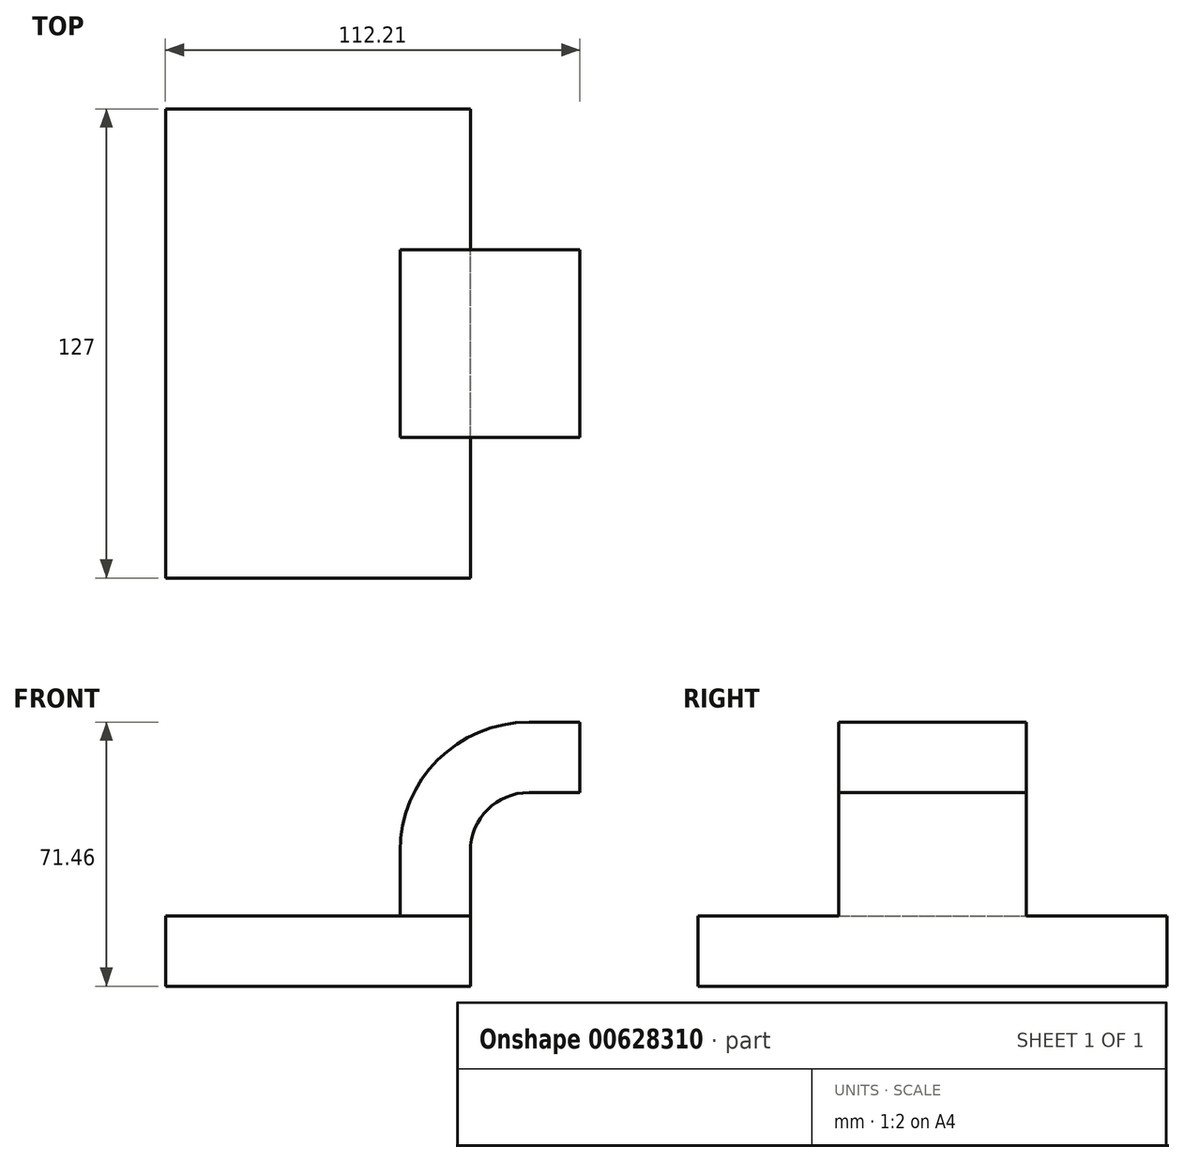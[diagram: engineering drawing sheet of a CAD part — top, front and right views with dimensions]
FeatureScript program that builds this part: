
annotation { "Feature Type Name" : "Feature", "Feature Type Description" : "" }
export const myFeature = defineFeature(function(context is Context, id is Id, definition is map)
    precondition{}
    {
        {
            var Q0;
            Q0=qCreatedBy(makeId("Front.planeOp"),FACE);
            var sketch = newSketch(context, id + "F0", { "sketchPlane" : qUnion([Q0])});
            skLineSegment(sketch, "E0.bottom", {"start": v(41.28, -9.52) * mm, "end": v(-41.28, -9.53) * mm});
            skLineSegment(sketch, "E0.top", {"start": v(41.28, 9.53) * mm, "end": v(-41.28, 9.53) * mm});
            skLineSegment(sketch, "E0.left", {"start": v(41.28, -9.52) * mm, "end": v(41.28, 9.53) * mm});
            skLineSegment(sketch, "E0.right", {"start": v(-41.28, -9.53) * mm, "end": v(-41.28, 9.53) * mm});
            skPoint(sketch, "E0.middle", {"position": v(0, 0) * mm});
            skLineSegment(sketch, "E1.bottom", {"start": v(70.93, 66.68) * mm, "end": v(121.73, 66.68) * mm});
            skLineSegment(sketch, "E1.top", {"start": v(70.93, 38.1) * mm, "end": v(121.73, 38.1) * mm});
            skLineSegment(sketch, "E1.left", {"start": v(121.73, 38.1) * mm, "end": v(121.73, 66.68) * mm});
            skLineSegment(sketch, "E1.right", {"start": v(70.93, 38.1) * mm, "end": v(70.93, 66.68) * mm});
            skPoint(sketch, "E1.middle", {"position": v(96.33, 52.39) * mm});
            skLineSegment(sketch, "E2", {"start": v(41.28, 9.53) * mm, "end": v(41.28, 27) * mm});
            skArc(sketch, "E3", {"start": v(41.27, 27) * mm, "mid": v(45.92, 38.23) * mm, "end": v(57.15, 42.88) * mm});
            skLineSegment(sketch, "E4", {"start": v(57.15, 42.88) * mm, "end": v(85.73, 42.88) * mm});
            skLineSegment(sketch, "E5.0", {"start": v(57.15, 61.93) * mm, "end": v(85.73, 61.93) * mm});
            skArc(sketch, "E5.1", {"start": v(22.23, 27) * mm, "mid": v(32.45, 51.7) * mm, "end": v(57.15, 61.93) * mm});
            skLineSegment(sketch, "E5.2", {"start": v(22.22, 9.53) * mm, "end": v(22.22, 27) * mm});
            skLineSegment(sketch, "E6", {"start": v(85.73, 42.88) * mm, "end": v(85.73, 61.93) * mm});
            skFitSpline(sketch, "E7", {"points": [v(-41.28, 9.53) * mm, v(57.15, 61.93) * mm], "startDerivative": vector(-10.9, 62.98) * mm, "endDerivative": vector(59.29, -31.03) * mm});
            skSolve(sketch);
        }
        {
            var Q0;
            {var subQ1=sQuery(id+"F0.wireOp",EDGE,"E2");Q0=makeQuery(id+"F0.imprint","IMPRINT",FACE,{"disambiguationData":[TD([[makeQuery(id+"F0.imprint","IMPRINT",EDGE,{"derivedFrom":subQ1}),1.0]])]});}
            var sketch = newSketch(context, id + "F1", { "sketchPlane" : qUnion([Q0])});
            skSolve(sketch);
        }
        {
            var Q0;
            Q0=makeQuery(id+"F0.imprint","IMPRINT",FACE,{"disambiguationData":[TD([[makeQuery(id+"F0.imprint","IMPRINT",EDGE,{"derivedFrom":sQuery(id+"F0.wireOp",EDGE,"E0.bottom")}),-1.0]])]});
            extrude(context, id + "F2", {"entities" : qUnion([Q0]), "endBound" : BoundingType.SYMMETRIC, "depth" : 127 * mm, "offsetDistance" : 25.4 * mm});
        }
        {
            var Q0;
            {var subQ1=sQuery(id+"F0.wireOp",EDGE,"E2");Q0=makeQuery(id+"F1.imprint","IMPRINT",FACE,{"disambiguationData":[TD([[makeQuery(id+"F1.imprint","IMPRINT",EDGE,{"derivedFrom":makeQuery(id+"F0.imprint","IMPRINT",EDGE,{"derivedFrom":subQ1})}),1.0]])]});}
            extrude(context, id + "F3", {"entities" : qUnion([Q0]), "operationType" : NewBodyOperationType.ADD, "endBound" : BoundingType.SYMMETRIC, "depth" : 50.8 * mm, "offsetDistance" : 25.4 * mm});
        }
    });
